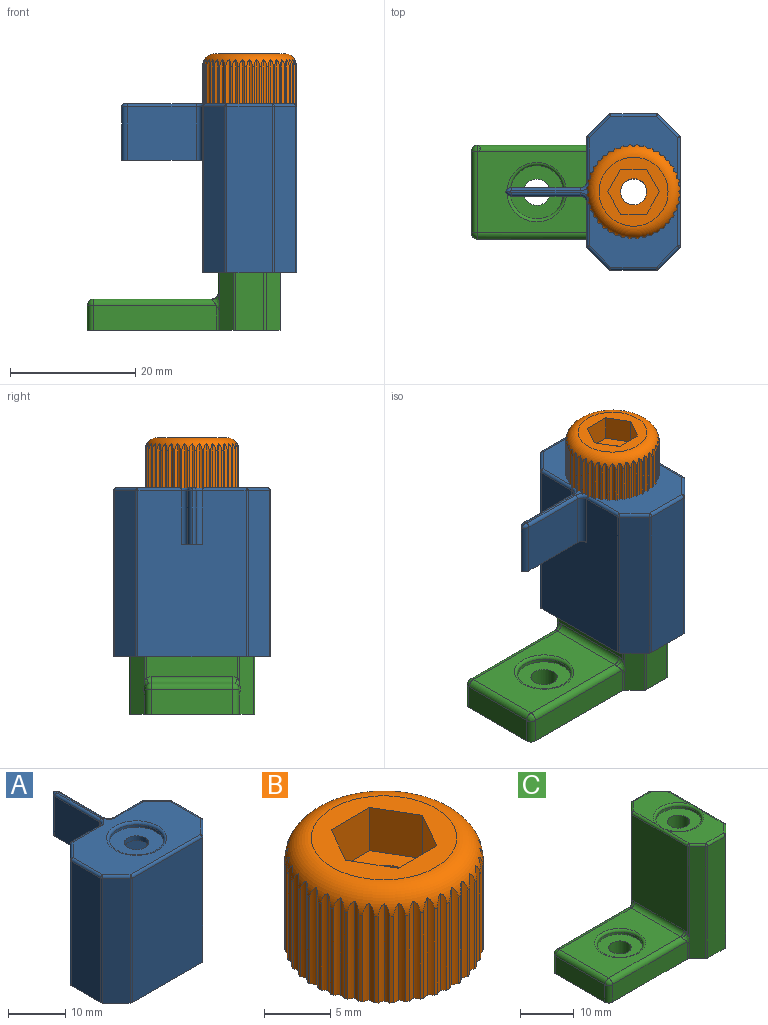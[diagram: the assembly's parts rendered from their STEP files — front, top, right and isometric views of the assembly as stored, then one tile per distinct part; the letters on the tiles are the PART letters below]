
ASSEMBLY  parts=3 mates=2
PART A: 69 faces, bbox 25x28x27 mm
  f0: plane 26.5x17.24mm, normal (0,1,0), area 428.9mm2, adj f2,f28,f35,f40,f42,f43,f61,f62
  f1: cylinder r=2.1mm len=4.2mm, axis (0,0,1), area 13.2mm2, adj f19,f37
  f2: plane 25x15mm, normal (0,0,-1), area 138.2mm2, adj f0,f3,f4,f5,f6,f7,f8,f9
  f3: plane 26.5x3.38mm, normal (-0.71,0.71,0), area 126.6mm2, adj f2,f28,f29,f57
  f4: plane 26.5x7.24mm, normal (-1,0,0), area 191.9mm2, adj f2,f29,f30,f53
  f5: plane 26.5x3.38mm, normal (-0.71,-0.71,0), area 126.6mm2, adj f2,f30,f31,f49
  f6: plane 26.5x17.24mm, normal (0,-1,0), area 456.9mm2, adj f2,f31,f32,f46
  f7: plane 26.5x3.38mm, normal (0.71,-0.71,0), area 126.6mm2, adj f2,f32,f33,f50
  f8: plane 26.5x7.24mm, normal (1,0,0), area 191.9mm2, adj f2,f33,f34,f54
  f9: plane 26.5x3.38mm, normal (0.71,0.71,0), area 126.6mm2, adj f2,f34,f35,f58
  f10: plane 26.86x24mm, normal (0,0,1), area 232.5mm2, adj f38,f46,f49,f50,f53,f54,f57,f58
  f11: plane 25x15.46mm, normal (0,1,0), area 386.5mm2, adj f2,f19,f20,f27
  f12: plane 25x2.12mm, normal (-0.71,0.71,0), area 74.9mm2, adj f2,f19,f20,f21
  f13: plane 25x5.46mm, normal (-1,0,0), area 136.5mm2, adj f2,f19,f21,f22
  f14: plane 25x2.12mm, normal (-0.71,-0.71,0), area 74.9mm2, adj f2,f19,f22,f23
  f15: plane 25x15.46mm, normal (0,-1,0), area 386.5mm2, adj f2,f19,f23,f24
  f16: plane 25x2.12mm, normal (0.71,-0.71,0), area 74.9mm2, adj f2,f19,f24,f25
  f17: plane 25x5.46mm, normal (1,0,0), area 136.5mm2, adj f2,f19,f25,f26
  f18: plane 25x2.12mm, normal (0.71,0.71,0), area 74.9mm2, adj f2,f19,f26,f27
  f19: plane 20.7x10.7mm, normal (0,0,-1), area 196mm2, adj f1,f11,f12,f13,f14,f15,f16,f17
  f20: cylinder r=0.5mm len=25mm, axis (0,0,1), area 9.8mm2, adj f2,f11,f12,f19
  f21: cylinder r=0.5mm len=25mm, axis (0,0,1), area 9.8mm2, adj f2,f12,f13,f19
  f22: cylinder r=0.5mm len=25mm, axis (0,0,1), area 9.8mm2, adj f2,f13,f14,f19
  f23: cylinder r=0.5mm len=25mm, axis (0,0,-1), area 9.8mm2, adj f2,f14,f15,f19
  f24: cylinder r=0.5mm len=25mm, axis (0,0,1), area 9.8mm2, adj f2,f15,f16,f19
  f25: cylinder r=0.5mm len=25mm, axis (0,0,1), area 9.8mm2, adj f2,f16,f17,f19
  f26: cylinder r=0.5mm len=25mm, axis (0,0,1), area 9.8mm2, adj f2,f17,f18,f19
  f27: cylinder r=0.5mm len=25mm, axis (0,0,-1), area 9.8mm2, adj f2,f11,f18,f19
  f28: cylinder r=0.5mm len=26.5mm, axis (0,0,-1), area 10.4mm2, adj f0,f2,f3,f59
  f29: cylinder r=0.5mm len=26.5mm, axis (0,0,1), area 10.4mm2, adj f2,f3,f4,f55
  f30: cylinder r=0.5mm len=26.5mm, axis (0,0,-1), area 10.4mm2, adj f2,f4,f5,f51
  f31: cylinder r=0.5mm len=26.5mm, axis (0,0,-1), area 10.4mm2, adj f2,f5,f6,f47
  f32: cylinder r=0.5mm len=26.5mm, axis (0,0,-1), area 10.4mm2, adj f2,f6,f7,f48
  f33: cylinder r=0.5mm len=26.5mm, axis (0,0,1), area 10.4mm2, adj f2,f7,f8,f52
  f34: cylinder r=0.5mm len=26.5mm, axis (0,0,-1), area 10.4mm2, adj f2,f8,f9,f56
  f35: cylinder r=0.5mm len=26.5mm, axis (0,0,-1), area 10.4mm2, adj f0,f2,f9,f60
  f36: cylinder r=4.72mm len=9.43mm, axis (0,0,1), area 14.8mm2, adj f37,f38
  f37: plane 9.43x9.43mm, normal (0,0,1), area 56mm2, adj f1,f36
  f38: torus R=5.22mm, axis (0,0,1), area 24.2mm2, adj f10,f36
  f39: plane 11x8.5mm, normal (1,0,0), area 93.5mm2, adj f40,f42,f45,f66
  f40: plane 12.94x3.3mm, normal (0,0,-1), area 16.9mm2, adj f0,f39,f41,f42,f43,f44,f45
  f41: plane 11x8.5mm, normal (-1,0,0), area 93.5mm2, adj f40,f43,f44,f65
  f42: cylinder r=1mm len=8.5mm, axis (0,0,-1), area 13.4mm2, adj f0,f39,f40,f64
  f43: cylinder r=1mm len=8.5mm, axis (0,0,1), area 13.4mm2, adj f0,f40,f41,f63
  f44: cylinder r=1mm len=8.5mm, axis (0,0,-1), area 10.3mm2, adj f40,f41,f45,f67
  f45: cylinder r=1mm len=8.5mm, axis (0,0,1), area 10.3mm2, adj f39,f40,f44,f68
  f46: cylinder r=0.5mm len=17.24mm, axis (-1,0,0), area 13.5mm2, adj f6,f10,f47,f48
  f47: sphere r=0.5mm, area 0.2mm2, adj f31,f46,f49
  f48: sphere r=0.5mm, area 0.2mm2, adj f32,f46,f50
  f49: cylinder r=0.5mm len=3.73mm, axis (-0.71,0.71,0), area 3.8mm2, adj f5,f10,f47,f51
  f50: cylinder r=0.5mm len=3.73mm, axis (-0.71,-0.71,0), area 3.8mm2, adj f7,f10,f48,f52
  f51: sphere r=0.5mm, area 0.2mm2, adj f30,f49,f53
  f52: sphere r=0.5mm, area 0.2mm2, adj f33,f50,f54
  f53: cylinder r=0.5mm len=7.24mm, axis (0,1,0), area 5.7mm2, adj f4,f10,f51,f55
  f54: cylinder r=0.5mm len=7.24mm, axis (0,-1,0), area 5.7mm2, adj f8,f10,f52,f56
  f55: sphere r=0.5mm, area 0.2mm2, adj f29,f53,f57
  f56: sphere r=0.5mm, area 0.2mm2, adj f34,f54,f58
  f57: cylinder r=0.5mm len=3.73mm, axis (0.71,0.71,0), area 3.8mm2, adj f3,f10,f55,f59
  f58: cylinder r=0.5mm len=3.73mm, axis (0.71,-0.71,0), area 3.8mm2, adj f9,f10,f56,f60
  f59: sphere r=0.5mm, area 0.2mm2, adj f28,f57,f61
  f60: sphere r=0.5mm, area 0.2mm2, adj f35,f58,f62
  f61: cylinder r=0.5mm len=6.97mm, axis (1,0,0), area 5.5mm2, adj f0,f10,f59,f63
  f62: cylinder r=0.5mm len=6.97mm, axis (1,0,0), area 5.5mm2, adj f0,f10,f60,f64
  f63: torus R=1.5mm, axis (0,0,1), area 1.5mm2, adj f10,f43,f61,f65
  f64: torus R=1.5mm, axis (0,0,1), area 1.5mm2, adj f10,f42,f62,f66
  f65: cylinder r=0.5mm len=11mm, axis (0,-1,0), area 8.6mm2, adj f10,f41,f63,f67
  f66: cylinder r=0.5mm len=11mm, axis (0,1,0), area 8.6mm2, adj f10,f39,f64,f68
  f67: torus R=0.5mm, axis (0,0,1), area 0.7mm2, adj f10,f44,f65,f68
  f68: torus R=0.5mm, axis (0,0,1), area 0.7mm2, adj f10,f45,f66,f67
PART B: 131 faces, bbox 16.2x16.2x10 mm
  f0: cylinder r=2.1mm len=6mm, axis (0,0,-1), area 79.2mm2, adj f40,f130
  f1: cylinder r=7.5mm len=8mm, axis (0,0,-1), area 2.4mm2, adj f40,f41,f121,f122
  f2: cylinder r=7.5mm len=8mm, axis (0,0,-1), area 2.4mm2, adj f40,f41,f119,f120
  f3: cylinder r=7.5mm len=8mm, axis (0,0,-1), area 2.4mm2, adj f40,f41,f117,f118
  f4: cylinder r=7.5mm len=8mm, axis (0,0,-1), area 2.4mm2, adj f40,f41,f115,f116
  f5: cylinder r=7.5mm len=8mm, axis (0,0,-1), area 2.4mm2, adj f40,f41,f113,f114
  f6: cylinder r=7.5mm len=8mm, axis (0,0,-1), area 2.4mm2, adj f40,f41,f111,f112
  f7: cylinder r=7.5mm len=8mm, axis (0,0,-1), area 2.4mm2, adj f40,f41,f109,f110
  f8: cylinder r=7.5mm len=8mm, axis (0,0,-1), area 2.4mm2, adj f40,f41,f107,f108
  f9: cylinder r=7.5mm len=8mm, axis (0,0,-1), area 2.4mm2, adj f40,f41,f105,f106
  f10: cylinder r=7.5mm len=8mm, axis (0,0,-1), area 2.4mm2, adj f40,f41,f103,f104
  f11: cylinder r=7.5mm len=8mm, axis (0,0,-1), area 2.4mm2, adj f40,f41,f101,f102
  f12: cylinder r=7.5mm len=8mm, axis (0,0,-1), area 2.4mm2, adj f40,f41,f99,f100
  f13: cylinder r=7.5mm len=8mm, axis (0,0,-1), area 2.4mm2, adj f40,f41,f97,f98
  f14: cylinder r=7.5mm len=8mm, axis (0,0,-1), area 2.4mm2, adj f40,f41,f95,f96
  f15: cylinder r=7.5mm len=8mm, axis (0,0,-1), area 2.4mm2, adj f40,f41,f93,f94
  f16: cylinder r=7.5mm len=8mm, axis (0,0,-1), area 2.4mm2, adj f40,f41,f91,f92
  f17: cylinder r=7.5mm len=8mm, axis (0,0,-1), area 2.4mm2, adj f40,f41,f89,f90
  f18: cylinder r=7.5mm len=8mm, axis (0,0,-1), area 2.4mm2, adj f40,f41,f87,f88
  f19: cylinder r=7.5mm len=8mm, axis (0,0,-1), area 2.4mm2, adj f40,f41,f85,f86
  f20: cylinder r=7.5mm len=8mm, axis (0,0,-1), area 2.4mm2, adj f40,f41,f83,f84
  f21: cylinder r=7.5mm len=8mm, axis (0,0,-1), area 2.4mm2, adj f40,f41,f81,f82
  f22: cylinder r=7.5mm len=8mm, axis (0,0,-1), area 2.4mm2, adj f40,f41,f79,f80
  f23: cylinder r=7.5mm len=8mm, axis (0,0,-1), area 2.4mm2, adj f40,f41,f77,f78
  f24: cylinder r=7.5mm len=8mm, axis (0,0,-1), area 2.4mm2, adj f40,f41,f75,f76
  f25: cylinder r=7.5mm len=8mm, axis (0,0,-1), area 2.4mm2, adj f40,f41,f73,f74
  f26: cylinder r=7.5mm len=8mm, axis (0,0,-1), area 2.4mm2, adj f40,f41,f71,f72
  f27: cylinder r=7.5mm len=8mm, axis (0,0,-1), area 2.4mm2, adj f40,f41,f69,f70
  f28: cylinder r=7.5mm len=8mm, axis (0,0,-1), area 2.4mm2, adj f40,f41,f67,f68
  f29: cylinder r=7.5mm len=8mm, axis (0,0,-1), area 2.4mm2, adj f40,f41,f65,f66
  f30: cylinder r=7.5mm len=8mm, axis (0,0,-1), area 2.4mm2, adj f40,f41,f62,f64
  f31: cylinder r=7.5mm len=8mm, axis (0,0,-1), area 2.4mm2, adj f40,f41,f61,f63
  f32: cylinder r=7.5mm len=8mm, axis (0,0,-1), area 2.4mm2, adj f40,f41,f45,f60
  f33: cylinder r=7.5mm len=8mm, axis (0,0,-1), area 2.4mm2, adj f40,f41,f58,f123
  f34: cylinder r=7.5mm len=8mm, axis (0,0,-1), area 2.4mm2, adj f40,f41,f56,f59
  f35: cylinder r=7.5mm len=8mm, axis (0,0,-1), area 2.4mm2, adj f40,f41,f54,f57
  f36: cylinder r=7.5mm len=8mm, axis (0,0,-1), area 2.4mm2, adj f40,f41,f52,f55
  f37: cylinder r=7.5mm len=8mm, axis (0,0,-1), area 2.4mm2, adj f40,f41,f50,f53
  f38: cylinder r=7.5mm len=8mm, axis (0,0,-1), area 2.4mm2, adj f40,f41,f48,f51
  f39: cylinder r=7.5mm len=8mm, axis (0,0,-1), area 2.4mm2, adj f40,f41,f46,f49
  f40: plane 14.97x14.97mm, normal (0,0,-1), area 157.5mm2, adj f0,f1,f2,f3,f4,f5,f6,f7
  f41: torus R=5.5mm, axis (0,0,1), area 107.2mm2, adj f1,f2,f3,f4,f5,f6,f7,f8
  f42: cylinder r=7.5mm len=8mm, axis (0,0,-1), area 2.4mm2, adj f40,f41,f44,f47
  f43: plane 11x11mm, normal (0,0,1), area 50.7mm2, adj f41,f124,f125,f126,f127,f128,f129
  f44: cylinder r=1.32mm len=8.99mm, axis (0,0,1), area 4.4mm2, adj f40,f41,f42,f45
  f45: cylinder r=1.32mm len=8.99mm, axis (0,0,1), area 4.4mm2, adj f32,f40,f41,f44
  f46: cylinder r=1.32mm len=8.99mm, axis (0,0,1), area 4.4mm2, adj f39,f40,f41,f47
  f47: cylinder r=1.32mm len=8.99mm, axis (0,0,1), area 4.4mm2, adj f40,f41,f42,f46
  f48: cylinder r=1.32mm len=8.99mm, axis (0,0,1), area 4.4mm2, adj f38,f40,f41,f49
  f49: cylinder r=1.32mm len=8.99mm, axis (0,0,1), area 4.4mm2, adj f39,f40,f41,f48
  f50: cylinder r=1.32mm len=8.99mm, axis (0,0,1), area 4.4mm2, adj f37,f40,f41,f51
  f51: cylinder r=1.32mm len=8.99mm, axis (0,0,1), area 4.4mm2, adj f38,f40,f41,f50
  f52: cylinder r=1.32mm len=8.99mm, axis (0,0,1), area 4.4mm2, adj f36,f40,f41,f53
  f53: cylinder r=1.32mm len=8.99mm, axis (0,0,1), area 4.4mm2, adj f37,f40,f41,f52
  f54: cylinder r=1.32mm len=8.99mm, axis (0,0,1), area 4.4mm2, adj f35,f40,f41,f55
  f55: cylinder r=1.32mm len=8.99mm, axis (0,0,1), area 4.4mm2, adj f36,f40,f41,f54
  f56: cylinder r=1.32mm len=8.99mm, axis (0,0,1), area 4.4mm2, adj f34,f40,f41,f57
  f57: cylinder r=1.32mm len=8.99mm, axis (0,0,1), area 4.4mm2, adj f35,f40,f41,f56
  f58: cylinder r=1.32mm len=8.99mm, axis (0,0,1), area 4.4mm2, adj f33,f40,f41,f59
  f59: cylinder r=1.32mm len=8.99mm, axis (0,0,1), area 4.4mm2, adj f34,f40,f41,f58
  f60: cylinder r=1.32mm len=8.99mm, axis (0,0,1), area 4.4mm2, adj f32,f40,f41,f61
  f61: cylinder r=1.32mm len=8.99mm, axis (0,0,1), area 4.4mm2, adj f31,f40,f41,f60
  f62: cylinder r=1.32mm len=8.99mm, axis (0,0,1), area 4.4mm2, adj f30,f40,f41,f63
  f63: cylinder r=1.32mm len=8.99mm, axis (0,0,1), area 4.4mm2, adj f31,f40,f41,f62
  f64: cylinder r=1.32mm len=8.99mm, axis (0,0,1), area 4.4mm2, adj f30,f40,f41,f65
  f65: cylinder r=1.32mm len=8.99mm, axis (0,0,1), area 4.4mm2, adj f29,f40,f41,f64
  f66: cylinder r=1.32mm len=8.99mm, axis (0,0,1), area 4.4mm2, adj f29,f40,f41,f67
  f67: cylinder r=1.32mm len=8.99mm, axis (0,0,1), area 4.4mm2, adj f28,f40,f41,f66
  f68: cylinder r=1.32mm len=8.99mm, axis (0,0,1), area 4.4mm2, adj f28,f40,f41,f69
  f69: cylinder r=1.32mm len=8.99mm, axis (0,0,1), area 4.4mm2, adj f27,f40,f41,f68
  f70: cylinder r=1.32mm len=8.99mm, axis (0,0,1), area 4.4mm2, adj f27,f40,f41,f71
  f71: cylinder r=1.32mm len=8.99mm, axis (0,0,1), area 4.4mm2, adj f26,f40,f41,f70
  f72: cylinder r=1.32mm len=8.99mm, axis (0,0,1), area 4.4mm2, adj f26,f40,f41,f73
  f73: cylinder r=1.32mm len=8.99mm, axis (0,0,1), area 4.4mm2, adj f25,f40,f41,f72
  f74: cylinder r=1.32mm len=8.99mm, axis (0,0,1), area 4.4mm2, adj f25,f40,f41,f75
  f75: cylinder r=1.32mm len=8.99mm, axis (0,0,1), area 4.4mm2, adj f24,f40,f41,f74
  f76: cylinder r=1.32mm len=8.99mm, axis (0,0,1), area 4.4mm2, adj f24,f40,f41,f77
  f77: cylinder r=1.32mm len=8.99mm, axis (0,0,1), area 4.4mm2, adj f23,f40,f41,f76
  f78: cylinder r=1.32mm len=8.99mm, axis (0,0,1), area 4.4mm2, adj f23,f40,f41,f79
  f79: cylinder r=1.32mm len=8.99mm, axis (0,0,1), area 4.4mm2, adj f22,f40,f41,f78
  f80: cylinder r=1.32mm len=8.99mm, axis (0,0,1), area 4.4mm2, adj f22,f40,f41,f81
  f81: cylinder r=1.32mm len=8.99mm, axis (0,0,1), area 4.4mm2, adj f21,f40,f41,f80
  f82: cylinder r=1.32mm len=8.99mm, axis (0,0,1), area 4.4mm2, adj f21,f40,f41,f83
  f83: cylinder r=1.32mm len=8.99mm, axis (0,0,1), area 4.4mm2, adj f20,f40,f41,f82
  f84: cylinder r=1.32mm len=8.99mm, axis (0,0,1), area 4.4mm2, adj f20,f40,f41,f85
  f85: cylinder r=1.32mm len=8.99mm, axis (0,0,1), area 4.4mm2, adj f19,f40,f41,f84
  f86: cylinder r=1.32mm len=8.99mm, axis (0,0,1), area 4.4mm2, adj f19,f40,f41,f87
  f87: cylinder r=1.32mm len=8.99mm, axis (0,0,1), area 4.4mm2, adj f18,f40,f41,f86
  f88: cylinder r=1.32mm len=8.99mm, axis (0,0,1), area 4.4mm2, adj f18,f40,f41,f89
  f89: cylinder r=1.32mm len=8.99mm, axis (0,0,1), area 4.4mm2, adj f17,f40,f41,f88
  f90: cylinder r=1.32mm len=8.99mm, axis (0,0,1), area 4.4mm2, adj f17,f40,f41,f91
  f91: cylinder r=1.32mm len=8.99mm, axis (0,0,1), area 4.4mm2, adj f16,f40,f41,f90
  f92: cylinder r=1.32mm len=8.99mm, axis (0,0,1), area 4.4mm2, adj f16,f40,f41,f93
  f93: cylinder r=1.32mm len=8.99mm, axis (0,0,1), area 4.4mm2, adj f15,f40,f41,f92
  f94: cylinder r=1.32mm len=8.99mm, axis (0,0,1), area 4.4mm2, adj f15,f40,f41,f95
  f95: cylinder r=1.32mm len=8.99mm, axis (0,0,1), area 4.4mm2, adj f14,f40,f41,f94
  f96: cylinder r=1.32mm len=8.99mm, axis (0,0,1), area 4.4mm2, adj f14,f40,f41,f97
  f97: cylinder r=1.32mm len=8.99mm, axis (0,0,1), area 4.4mm2, adj f13,f40,f41,f96
  f98: cylinder r=1.32mm len=8.99mm, axis (0,0,1), area 4.4mm2, adj f13,f40,f41,f99
  f99: cylinder r=1.32mm len=8.99mm, axis (0,0,1), area 4.4mm2, adj f12,f40,f41,f98
  f100: cylinder r=1.32mm len=8.99mm, axis (0,0,1), area 4.4mm2, adj f12,f40,f41,f101
  f101: cylinder r=1.32mm len=8.99mm, axis (0,0,1), area 4.4mm2, adj f11,f40,f41,f100
  f102: cylinder r=1.32mm len=8.99mm, axis (0,0,1), area 4.4mm2, adj f11,f40,f41,f103
  f103: cylinder r=1.32mm len=8.99mm, axis (0,0,1), area 4.4mm2, adj f10,f40,f41,f102
  f104: cylinder r=1.32mm len=8.99mm, axis (0,0,1), area 4.4mm2, adj f10,f40,f41,f105
  f105: cylinder r=1.32mm len=8.99mm, axis (0,0,1), area 4.4mm2, adj f9,f40,f41,f104
  f106: cylinder r=1.32mm len=8.99mm, axis (0,0,1), area 4.4mm2, adj f9,f40,f41,f107
  f107: cylinder r=1.32mm len=8.99mm, axis (0,0,1), area 4.4mm2, adj f8,f40,f41,f106
  f108: cylinder r=1.32mm len=8.99mm, axis (0,0,1), area 4.4mm2, adj f8,f40,f41,f109
  f109: cylinder r=1.32mm len=8.99mm, axis (0,0,1), area 4.4mm2, adj f7,f40,f41,f108
  f110: cylinder r=1.32mm len=8.99mm, axis (0,0,1), area 4.4mm2, adj f7,f40,f41,f111
  f111: cylinder r=1.32mm len=8.99mm, axis (0,0,1), area 4.4mm2, adj f6,f40,f41,f110
  f112: cylinder r=1.32mm len=8.99mm, axis (0,0,1), area 4.4mm2, adj f6,f40,f41,f113
  f113: cylinder r=1.32mm len=8.99mm, axis (0,0,1), area 4.4mm2, adj f5,f40,f41,f112
  f114: cylinder r=1.32mm len=8.99mm, axis (0,0,1), area 4.4mm2, adj f5,f40,f41,f115
  f115: cylinder r=1.32mm len=8.99mm, axis (0,0,1), area 4.4mm2, adj f4,f40,f41,f114
  f116: cylinder r=1.32mm len=8.99mm, axis (0,0,1), area 4.4mm2, adj f4,f40,f41,f117
  f117: cylinder r=1.32mm len=8.99mm, axis (0,0,1), area 4.4mm2, adj f3,f40,f41,f116
  f118: cylinder r=1.32mm len=8.99mm, axis (0,0,1), area 4.4mm2, adj f3,f40,f41,f119
  f119: cylinder r=1.32mm len=8.99mm, axis (0,0,1), area 4.4mm2, adj f2,f40,f41,f118
  f120: cylinder r=1.32mm len=8.99mm, axis (0,0,1), area 4.4mm2, adj f2,f40,f41,f121
  f121: cylinder r=1.32mm len=8.99mm, axis (0,0,1), area 4.4mm2, adj f1,f40,f41,f120
  f122: cylinder r=1.32mm len=8.99mm, axis (0,0,1), area 4.4mm2, adj f1,f40,f41,f123
  f123: cylinder r=1.32mm len=8.99mm, axis (0,0,1), area 4.4mm2, adj f33,f40,f41,f122
  f124: plane 4x3.58mm, normal (0.87,-0.5,0), area 16.5mm2, adj f43,f125,f129,f130
  f125: plane 4x3.57mm, normal (0.86,0.5,0), area 16.5mm2, adj f43,f124,f126,f130
  f126: plane 4.13x4mm, normal (0,1,0), area 16.5mm2, adj f43,f125,f127,f130
  f127: plane 4x3.58mm, normal (-0.87,0.5,0), area 16.5mm2, adj f43,f126,f128,f130
  f128: plane 4x3.57mm, normal (-0.86,-0.5,0), area 16.5mm2, adj f43,f127,f129,f130
  f129: plane 4.13x4mm, normal (0,-1,0), area 16.5mm2, adj f43,f124,f128,f130
  f130: plane 8.26x7.17mm, normal (0,0,1), area 30.5mm2, adj f0,f124,f125,f126,f127,f128,f129
PART C: 67 faces, bbox 31.5x20.1x26.1 mm
  f0: cylinder r=2.1mm len=4.2mm, axis (0,0,1), area 54.2mm2, adj f19,f62
  f1: plane 25.5x14.59mm, normal (1,0,0), area 348.9mm2, adj f13,f35,f36,f43,f62,f63,f64,f65
  f2: cylinder r=2.1mm len=4.2mm, axis (0,0,1), area 52.8mm2, adj f13,f60
  f3: plane 9x8.01mm, normal (0,0,1), area 45.8mm2, adj f25,f30,f37,f42,f43,f44
  f4: cylinder r=2.1mm len=17.69mm, axis (0,0,1), area 233.5mm2, adj f13,f63
  f5: plane 25.57x2.28mm, normal (-0.71,0.71,0), area 79.8mm2, adj f13,f21,f32,f33,f46,f58
  f6: plane 19.66x14.59mm, normal (-1,0,0), area 284.5mm2, adj f31,f32,f42,f55,f56,f57
  f7: plane 25.57x2.28mm, normal (-0.71,-0.71,0), area 79.8mm2, adj f13,f20,f30,f31,f45,f54
  f8: plane 25.5x4.58mm, normal (0,-1,0), area 116.7mm2, adj f13,f20,f24,f25
  f9: plane 25.5x2.21mm, normal (0.71,-0.71,0), area 79.8mm2, adj f13,f24,f36,f37
  f10: plane 25.5x2.21mm, normal (0.71,0.71,0), area 79.8mm2, adj f13,f23,f34,f35
  f11: plane 25.5x4.58mm, normal (0,1,0), area 116.7mm2, adj f13,f21,f22,f23
  f12: plane 9x8.01mm, normal (0,0,1), area 45.8mm2, adj f22,f33,f34,f42,f43,f44
  f13: plane 30.88x20.01mm, normal (0,0,-1), area 472.6mm2, adj f1,f2,f4,f5,f7,f8,f9,f10
  f14: plane 13x4mm, normal (-1,0,0), area 52mm2, adj f13,f47,f50,f51
  f15: plane 19.69x4.01mm, normal (0,-1,0), area 78.7mm2, adj f13,f45,f50,f53,f54
  f16: plane 19.69x4.02mm, normal (0,1,0), area 78.7mm2, adj f13,f46,f47,f48,f58
  f17: plane 18.88x13mm, normal (0,0,1), area 174.7mm2, adj f48,f51,f53,f56,f61
  f18: cylinder r=4.24mm len=8.49mm, axis (0,0,1), area 13.3mm2, adj f19,f44
  f19: plane 8.49x8.49mm, normal (0,0,1), area 42.7mm2, adj f0,f18
  f20: cylinder r=0.5mm len=25.5mm, axis (0,0,1), area 10mm2, adj f7,f8,f13,f26
  f21: cylinder r=0.5mm len=25.5mm, axis (0,0,1), area 10mm2, adj f5,f11,f13,f27
  f22: cylinder r=0.5mm len=4.58mm, axis (1,0,0), area 3.6mm2, adj f11,f12,f27,f28
  f23: cylinder r=0.5mm len=25.5mm, axis (0,0,1), area 10mm2, adj f10,f11,f13,f28
  f24: cylinder r=0.5mm len=25.5mm, axis (0,0,-1), area 10mm2, adj f8,f9,f13,f29
  f25: cylinder r=0.5mm len=4.58mm, axis (-1,0,0), area 3.6mm2, adj f3,f8,f26,f29
  f26: sphere r=0.5mm, area 0.2mm2, adj f20,f25,f30
  f27: sphere r=0.5mm, area 0.2mm2, adj f21,f22,f33
  f28: sphere r=0.5mm, area 0.3mm2, adj f22,f23,f34
  f29: sphere r=0.5mm, area 0.2mm2, adj f24,f25,f37
  f30: cylinder r=0.5mm len=2.57mm, axis (-0.71,0.71,0), area 2.5mm2, adj f3,f7,f26,f38
  f31: cylinder r=0.5mm len=20.75mm, axis (0,0,-1), area 7.9mm2, adj f6,f7,f38,f54
  f32: cylinder r=0.5mm len=20.75mm, axis (0,0,1), area 7.9mm2, adj f5,f6,f39,f58
  f33: cylinder r=0.5mm len=2.57mm, axis (0.71,0.71,0), area 2.5mm2, adj f5,f12,f27,f39
  f34: cylinder r=0.5mm len=2.57mm, axis (0.71,-0.71,0), area 2.5mm2, adj f10,f12,f28,f40
  f35: cylinder r=0.5mm len=25.5mm, axis (0,0,1), area 10mm2, adj f1,f10,f13,f40
  f36: cylinder r=0.5mm len=25.5mm, axis (0,0,1), area 10mm2, adj f1,f9,f13,f41
  f37: cylinder r=0.5mm len=2.57mm, axis (-0.71,-0.71,0), area 2.5mm2, adj f3,f9,f29,f41
  f38: sphere r=0.5mm, area 0.2mm2, adj f30,f31,f42
  f39: sphere r=0.5mm, area 0.2mm2, adj f32,f33,f42
  f40: sphere r=0.5mm, area 0.1mm2, adj f34,f35,f43
  f41: sphere r=0.5mm, area 0.2mm2, adj f36,f37,f43
  f42: cylinder r=0.5mm len=14.59mm, axis (0,1,0), area 11.2mm2, adj f3,f6,f12,f38,f39,f44
  f43: cylinder r=0.5mm len=14.59mm, axis (0,-1,0), area 11.3mm2, adj f1,f3,f12,f40,f41,f44
  f44: torus R=4.74mm, axis (0,0,1), area 21.4mm2, adj f3,f12,f18,f42,f43
  f45: cylinder r=0.5mm len=3.76mm, axis (0,0,1), area 1.4mm2, adj f7,f13,f15,f54
  f46: cylinder r=0.5mm len=3.76mm, axis (0,0,1), area 1.4mm2, adj f5,f13,f16,f58
  f47: cylinder r=1mm len=4mm, axis (0,0,-1), area 6.3mm2, adj f13,f14,f16,f49
  f48: cylinder r=1mm len=19.49mm, axis (1,0,0), area 30mm2, adj f16,f17,f49,f57,f58
  f49: sphere r=1mm, area 2.1mm2, adj f47,f48,f51
  f50: cylinder r=1mm len=4mm, axis (0,0,1), area 6.3mm2, adj f13,f14,f15,f52
  f51: cylinder r=1mm len=13mm, axis (0,1,0), area 20.4mm2, adj f14,f17,f49,f52
  f52: sphere r=1mm, area 1.6mm2, adj f50,f51,f53
  f53: cylinder r=1mm len=19.49mm, axis (-1,0,0), area 30mm2, adj f15,f17,f52,f54,f55
  f54: bspline ~2.82x1.21mm, area 1.7mm2, adj f7,f15,f31,f45,f53,f55
  f55: torus R=2mm, axis (1,0,0), area 0.9mm2, adj f6,f53,f54,f56
  f56: cylinder r=1mm len=13mm, axis (0,-1,0), area 20.4mm2, adj f6,f17,f55,f57
  f57: torus R=2mm, axis (1,0,0), area 0.9mm2, adj f6,f48,f56,f58
  f58: bspline ~2.85x1.21mm, area 1.7mm2, adj f5,f16,f32,f46,f48,f57
  f59: cylinder r=4.25mm len=8.49mm, axis (0,0,1), area 13.3mm2, adj f60,f61
  f60: plane 8.49x8.49mm, normal (0,0,1), area 42.8mm2, adj f2,f59
  f61: torus R=4.75mm, axis (0,0,1), area 21.9mm2, adj f17,f59
  f62: plane 8.5x7.2mm, normal (0,0,-1), area 47.3mm2, adj f0,f1,f64,f65,f66
  f63: plane 8.5x7.2mm, normal (0,0,1), area 47.3mm2, adj f1,f4,f64,f65,f66
  f64: plane 8.5x3.2mm, normal (0,1,0), area 27.2mm2, adj f1,f62,f63,f66
  f65: plane 8.5x3.2mm, normal (0,-1,0), area 27.2mm2, adj f1,f62,f63,f66
  f66: plane 7.2x3.2mm, normal (1,0,0), area 23mm2, adj f62,f63,f64,f65
PLACE A rot(axis=(0,0,1),90deg) t=(-46.61,-28.58,36.86)mm
PLACE B t=(-46.61,-28.58,61.86)mm
PLACE C t=(-57.05,-28.58,27.7)mm
MATE revolute A.f1 <-> B.f0  axis (0,0,-1) through (-46.61,-28.58,61.86)mm
MATE slider A.f1 <-> C.f0  axis (0,0,1) through (-46.61,-28.58,62.86)mm
